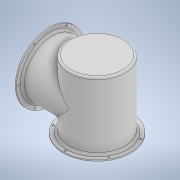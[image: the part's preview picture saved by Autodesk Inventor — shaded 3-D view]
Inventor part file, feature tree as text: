
AUTODESK INVENTOR PART (.ipt)
format: ipt  version: 2021 (Build 250183000, 183)  size: 317,440 bytes
history: native  units: mm
features: sketch x9, extrude x8, revolve x3, hole x3, plane x2, projected_geometry x2, fillet x1
ambient origin geometry x8: Origin, YZ Plane, XZ Plane, XY Plane, X Axis, Y Axis, Z Axis, Center Point
bodies: Solid1 (feature_tree)
feature tree (28):
  revolve  "Revolution1"  [1 undecoded]
  hole  "Hole1"  [1 undecoded]
  fillet  "Fillet1"  [1 undecoded]
  plane  "Work Plane1"
  sketch  "Sketch6"  dims[d10=16.0mm d11=3.0mm]
  extrude  "Extrusion3"  Depth=3.0mm
  extrude  "Extrusion5"  Depth=8.0mm
  extrude  "Extrusion4"  Depth=10.0mm
  revolve  "Revolution2"  [1 undecoded]
  extrude  "Extrusion6"  Depth=165.0mm
  hole  "Hole2"  [1 undecoded]
  extrude  "Extrusion7"  Depth=3.0mm TaperAngle=0.0deg
  plane  "Work Plane2"
  sketch  "Sketch12"  dims[d22=4.5mm d23=10.0mm d24=9.4mm d25=2.0mm d26=90.0deg d27=13.0mm d28=20.594885mm d29=4.5mm]
  extrude  "Extrusion9"  Depth=3.0mm TaperAngle=0.0deg
  extrude  "Extrusion10"  Depth=67.5mm
  extrude  "Extrusion11"  TaperAngle=90.0deg  [1 undecoded]
  revolve  "Revolution3"  [1 undecoded]
  hole  "Hole3"  [1 undecoded]
  sketch  "Sketch2"  dims[d3=90.0deg d5=81.5mm]
  projected_geometry  "Projected Loop1"
  sketch  "Sketch5"  dims[d7=9.0mm d8=5.0mm d9=45.0deg]
  projected_geometry  "Projected Loop6"
  sketch  "Sketch9"  dims[d16=4.5mm d17=8.0mm]
  sketch  "Sketch11"  dims[d18=60.0mm d20=360.0deg]
  sketch  "Sketch14"  dims[d32=2.0mm d33=5.0mm]
  sketch  "Sketch15"  dims[d34=165.0mm d43=9.0mm]
  sketch  "Sketch16"  dims[d50=135.0mm d51=10.0mm d52=0.0mm d53=112.0mm d54=0.0mm d56=48.0mm d57=0.0mm d59=67.5mm d60=90.0deg d62=5.0mm d63=45.0deg d65=48.0mm d66=0.0mm d67=48.0mm d68=0.0mm d74=2.0mm d75=3.0mm d76=67.5mm d78=2.0mm d79=4.5mm d80=4.5mm d81=60.0mm d83=360.0deg d85=4.5mm d86=6.0mm d87=6.3mm d88=2.0mm d89=90.0deg d90=8.0mm d91=20.594885mm d92=75.0mm d93=135.0mm d95=72.0mm d96=10.0mm d97=0.0mm d98=35.0mm d99=0.0mm d100=2.0mm d101=48.0mm d102=0.0mm d103=9.0mm d105=5.0mm d106=45.0deg d107=3.0mm d109=67.5mm d110=67.5mm d111=90.0deg d112=4.5mm d113=4.5mm d114=60.0mm d116=360.0deg d118=4.5mm d119=6.0mm d120=9.4mm d121=2.0mm d122=90.0deg d123=8.0mm d124=20.594885mm d125=3.0mm]
note: 8 required parameter values undecoded (feature->parameter linkage not recoverable at this tier; creation-order binding heuristic only, values carry confidence <= 0.55)